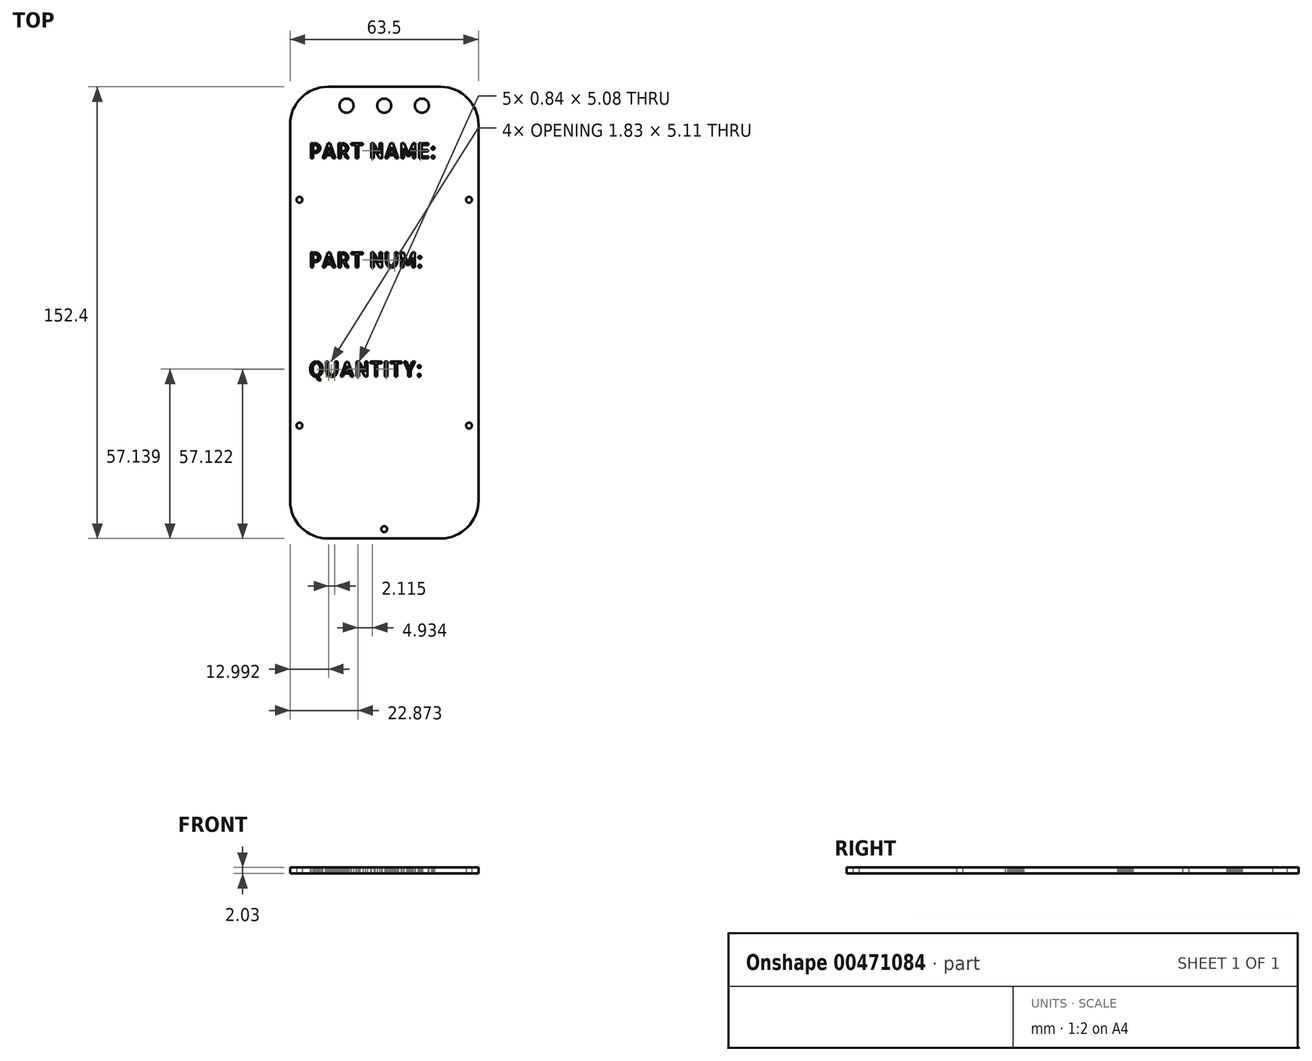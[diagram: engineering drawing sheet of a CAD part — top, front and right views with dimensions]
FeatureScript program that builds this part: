
annotation { "Feature Type Name" : "Feature", "Feature Type Description" : "" }
export const myFeature = defineFeature(function(context is Context, id is Id, definition is map)
    precondition{}
    {
        {
            var Q0;
            Q0=qCreatedBy(makeId("Top.planeOp"),FACE);
            var sketch = newSketch(context, id + "F0", { "sketchPlane" : qUnion([Q0])});
            skLineSegment(sketch, "E0.bottom", {"start": v(-19.05, 76.2) * mm, "end": v(19.05, 76.2) * mm});
            skLineSegment(sketch, "E0.top", {"start": v(-19.05, -76.2) * mm, "end": v(19.05, -76.2) * mm});
            skLineSegment(sketch, "E0.left", {"start": v(-31.75, 63.5) * mm, "end": v(-31.75, -63.5) * mm});
            skLineSegment(sketch, "E0.right", {"start": v(31.75, 63.5) * mm, "end": v(31.75, -63.5) * mm});
            skPoint(sketch, "E1", {"position": v(0, 76.2) * mm});
            skPoint(sketch, "E2", {"position": v(-31.75, 0) * mm});
            skCircle(sketch, "E3", {"center": v(0, 69.85) * mm, "radius": 2.38 * mm});
            skCircle(sketch, "E4", {"center": v(12.7, 69.85) * mm, "radius": 2.38 * mm});
            skCircle(sketch, "E5", {"center": v(-12.7, 69.85) * mm, "radius": 2.38 * mm});
            skCircle(sketch, "E6", {"center": v(28.58, 38.1) * mm, "radius": 1 * mm});
            skCircle(sketch, "E7", {"center": v(28.58, -38.1) * mm, "radius": 1 * mm});
            skCircle(sketch, "E8", {"center": v(-28.58, 38.1) * mm, "radius": 1 * mm});
            skCircle(sketch, "E9", {"center": v(-28.58, -38.1) * mm, "radius": 1 * mm});
            skPoint(sketch, "E10.visualSharp", {"position": v(-31.75, 76.2) * mm});
            skArc(sketch, "E10.filletArc", {"start": v(-19.05, 76.2) * mm, "mid": v(-28.03, 72.48) * mm, "end": v(-31.75, 63.5) * mm});
            skPoint(sketch, "E11.visualSharp", {"position": v(31.75, 76.2) * mm});
            skArc(sketch, "E11.filletArc", {"start": v(31.75, 63.5) * mm, "mid": v(28.03, 72.48) * mm, "end": v(19.05, 76.2) * mm});
            skPoint(sketch, "E12.visualSharp", {"position": v(31.75, -76.2) * mm});
            skArc(sketch, "E12.filletArc", {"start": v(19.05, -76.2) * mm, "mid": v(28.03, -72.48) * mm, "end": v(31.75, -63.5) * mm});
            skPoint(sketch, "E13.visualSharp", {"position": v(-31.75, -76.2) * mm});
            skArc(sketch, "E13.filletArc", {"start": v(-31.75, -63.5) * mm, "mid": v(-28.03, -72.48) * mm, "end": v(-19.05, -76.2) * mm});
            skText(sketch, "E14", { "text": "PART NAME:", "fontName": "AllertaStencil-Regular.ttf"});
            skText(sketch, "E15", { "text": "PART NUM:", "fontName": "AllertaStencil-Regular.ttf"});
            skText(sketch, "E16", { "text": "QUANTITY:", "fontName": "AllertaStencil-Regular.ttf"});
            skCircle(sketch, "E17", {"center": v(0, -73.03) * mm, "radius": 1 * mm});
            const initialGuessF0  = {"E14": [-0.0254, 0.05207, 1, 0, 0.00508], "E15": [-0.0254, 0.01524, 1, 0, 0.00508], "E16": [-0.0254, -0.0216, 1, 0, 0.00508]};
            skSetInitialGuess(sketch, initialGuessF0);
            skSolve(sketch);
        }
        {
            var Q0;
            Q0 = qSketchRegion(id + "F0", true);
            extrude(context, id + "F1", {"entities" : qUnion([Q0]), "depth" : 2.03 * mm});
        }
    });
